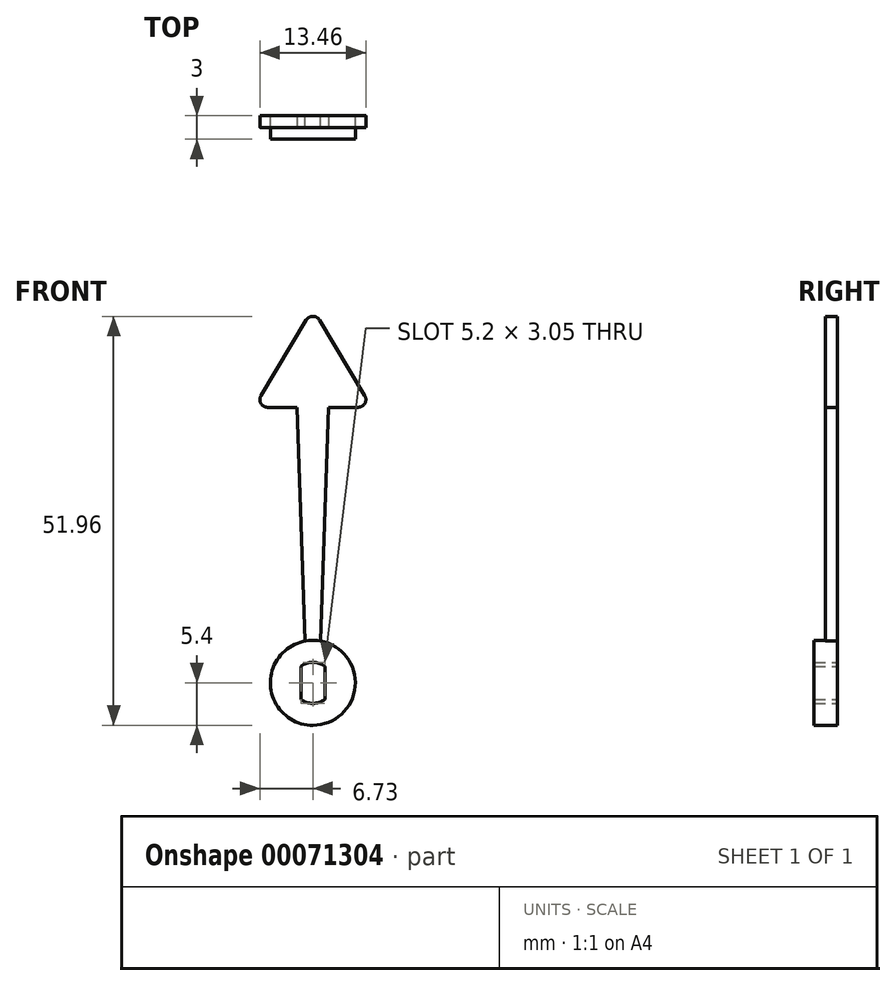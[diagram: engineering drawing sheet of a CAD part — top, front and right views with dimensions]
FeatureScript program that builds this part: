
annotation { "Feature Type Name" : "Feature", "Feature Type Description" : "" }
export const myFeature = defineFeature(function(context is Context, id is Id, definition is map)
    precondition{}
    {
        {
            var Q0;
            Q0=qCreatedBy(makeId("Front.planeOp"),FACE);
            var sketch = newSketch(context, id + "F0", { "sketchPlane" : qUnion([Q0])});
            skCircle(sketch, "E0", {"center": v(0, 0) * mm, "radius": 5.4 * mm});
            skCircle(sketch, "E1", {"center": v(0, 0) * mm, "radius": 2.6 * mm});
            skLineSegment(sketch, "E2", {"start": v(-1.52, 2.1) * mm, "end": v(-1.52, -2.1) * mm});
            skLineSegment(sketch, "E3", {"start": v(1.53, 2.1) * mm, "end": v(1.53, -2.1) * mm});
            skSolve(sketch);
        }
        {
            var Q0;
            {var subQ0=sQuery(id+"F0.wireOp",EDGE,"E2");Q0=makeQuery(id+"F0.imprint","IMPRINT",FACE,{"disambiguationData":[TD([[makeQuery(id+"F0.imprint","IMPRINT",EDGE,{"derivedFrom":subQ0}),-1.0]])]});}
            var Q1;
            Q1=makeQuery(id+"F0.imprint","IMPRINT",FACE,{"disambiguationData":[TD([[makeQuery(id+"F0.imprint","IMPRINT",EDGE,{"derivedFrom":sQuery(id+"F0.wireOp",EDGE,"E0")}),1.0]])]});
            var Q2;
            {var subQ0=sQuery(id+"F0.wireOp",EDGE,"E3");Q2=makeQuery(id+"F0.imprint","IMPRINT",FACE,{"disambiguationData":[TD([[makeQuery(id+"F0.imprint","IMPRINT",EDGE,{"derivedFrom":subQ0}),1.0]])]});}
            extrude(context, id + "F1", {"entities" : qUnion([Q0, Q1, Q2]), "endBound" : BoundingType.SYMMETRIC, "depth" : 3 * mm});
        }
        {
            var Q0;
            Q0=qCreatedBy(makeId("Front.planeOp"),FACE);
            var sketch = newSketch(context, id + "F2", { "sketchPlane" : qUnion([Q0])});
            skLineSegment(sketch, "E4", {"start": v(0, 0) * mm, "end": v(0, 35) * mm});
            skLineSegment(sketch, "E5", {"start": v(0, 35) * mm, "end": v(2, 35) * mm});
            skLineSegment(sketch, "E6", {"start": v(0, 4.34) * mm, "end": v(0.93, 4.34) * mm});
            skLineSegment(sketch, "E7", {"start": v(2, 35) * mm, "end": v(0.93, 4.34) * mm});
            skLineSegment(sketch, "E8.MirrorCS", {"start": v(-2, 35) * mm, "end": v(-0.93, 4.34) * mm});
            skLineSegment(sketch, "E9.MirrorCS", {"start": v(0, 35) * mm, "end": v(-2, 35) * mm});
            skLineSegment(sketch, "E10.MirrorCS", {"start": v(0, 4.34) * mm, "end": v(-0.93, 4.34) * mm});
            skSolve(sketch);
        }
        {
            var Q0;
            Q0=makeQuery(id+"F2.imprint","IMPRINT",FACE,{"disambiguationData":[TD([[makeQuery(id+"F2.imprint","IMPRINT",EDGE,{"derivedFrom":sQuery(id+"F2.wireOp",EDGE,"E8.MirrorCS")}),1.0]])]});
            var Q1;
            {var subQ0=sQuery(id+"F2.wireOp",EDGE,"E5");Q1=makeQuery(id+"F2.imprint","IMPRINT",FACE,{"disambiguationData":[TD([[makeQuery(id+"F2.imprint","IMPRINT",EDGE,{"derivedFrom":subQ0}),-1.0]])]});}
            var Q2;
            Q2=makeQuery(id+"F1.opExtrude","CAP_FACE",FACE,{"disambiguationData":[OSD([sQuery(id+"F0.wireOp",EDGE,"E0"),sQuery(id+"F0.wireOp",EDGE,"E1"),sQuery(id+"F0.wireOp",EDGE,"E2"),sQuery(id+"F0.wireOp",EDGE,"E3")])],"isStart":true});
            extrude(context, id + "F3", {"entities" : qUnion([Q0, Q1]), "operationType" : NewBodyOperationType.ADD, "endBound" : BoundingType.UP_TO_SURFACE, "oppositeDirection" : true, "endBoundEntityFace" : qUnion([Q2]), "depth" : 25 * mm});
        }
        {
            var Q0;
            Q0=qCreatedBy(makeId("Front.planeOp"),FACE);
            var sketch = newSketch(context, id + "F4", { "sketchPlane" : qUnion([Q0])});
            skLineSegment(sketch, "E11", {"start": v(0, 47.5) * mm, "end": v(0, 35) * mm});
            skLineSegment(sketch, "E12", {"start": v(-7.5, 35) * mm, "end": v(7.5, 35) * mm});
            skLineSegment(sketch, "E13", {"start": v(-7.5, 35) * mm, "end": v(0, 47.5) * mm});
            skLineSegment(sketch, "E14", {"start": v(0, 47.5) * mm, "end": v(7.5, 35) * mm});
            skSolve(sketch);
        }
        {
            var Q0;
            {var subQ0=sQuery(id+"F4.wireOp",EDGE,"E11");Q0=makeQuery(id+"F4.imprint","IMPRINT",FACE,{"disambiguationData":[TD([[makeQuery(id+"F4.imprint","IMPRINT",EDGE,{"derivedFrom":subQ0}),-1.0]])]});}
            var Q1;
            {var subQ0=sQuery(id+"F4.wireOp",EDGE,"E11");Q1=makeQuery(id+"F4.imprint","IMPRINT",FACE,{"disambiguationData":[TD([[makeQuery(id+"F4.imprint","IMPRINT",EDGE,{"derivedFrom":subQ0}),1.0]])]});}
            var Q2;
            Q2=makeQuery(id+"F3.boolean.opBoolean","MERGE",FACE,{"derivedFrom":[makeQuery(id+"F1.opExtrude","CAP_FACE",FACE,{"disambiguationData":[OSD([sQuery(id+"F0.wireOp",EDGE,"E0"),sQuery(id+"F0.wireOp",EDGE,"E1"),sQuery(id+"F0.wireOp",EDGE,"E2"),sQuery(id+"F0.wireOp",EDGE,"E3")])],"isStart":true}),makeQuery(id+"F3.opExtrude","CAP_FACE",FACE,{"disambiguationData":[OSD([sQuery(id+"F2.wireOp",EDGE,"E5"),sQuery(id+"F2.wireOp",EDGE,"E6"),sQuery(id+"F2.wireOp",EDGE,"E7"),sQuery(id+"F2.wireOp",EDGE,"E8.MirrorCS"),sQuery(id+"F2.wireOp",EDGE,"E9.MirrorCS"),sQuery(id+"F2.wireOp",EDGE,"E10.MirrorCS")])],"isStart":false})]});
            extrude(context, id + "F5", {"entities" : qUnion([Q0, Q1]), "operationType" : NewBodyOperationType.ADD, "endBound" : BoundingType.UP_TO_SURFACE, "oppositeDirection" : true, "endBoundEntityFace" : qUnion([Q2]), "depth" : 25 * mm});
        }
        {
            var Q0;
            Q0=makeQuery(id+"F5.opExtrude","SWEPT_EDGE",EDGE,{"disambiguationData":[OSD([sQuery(id+"F4.wireOp",EDGE,"E12"),sQuery(id+"F4.wireOp",EDGE,"E14")])]});
            fillet(context, id + "F6", {"entities" : qUnion([Q0]), "radius" : 1 * mm, "tangentPropagation" : true, "allowEdgeOverflow" : false});
        }
        {
            var Q0;
            Q0=makeQuery(id+"F5.opExtrude","SWEPT_EDGE",EDGE,{"disambiguationData":[OSD([sQuery(id+"F4.wireOp",EDGE,"E11"),sQuery(id+"F4.wireOp",EDGE,"E13"),sQuery(id+"F4.wireOp",EDGE,"E14")])]});
            fillet(context, id + "F7", {"entities" : qUnion([Q0]), "radius" : 1 * mm, "tangentPropagation" : true, "allowEdgeOverflow" : false});
        }
        {
            var Q0;
            Q0=makeQuery(id+"F5.opExtrude","SWEPT_EDGE",EDGE,{"disambiguationData":[OSD([sQuery(id+"F4.wireOp",EDGE,"E12"),sQuery(id+"F4.wireOp",EDGE,"E13")])]});
            fillet(context, id + "F8", {"entities" : qUnion([Q0]), "radius" : 1 * mm, "tangentPropagation" : true, "allowEdgeOverflow" : false});
        }
    });
